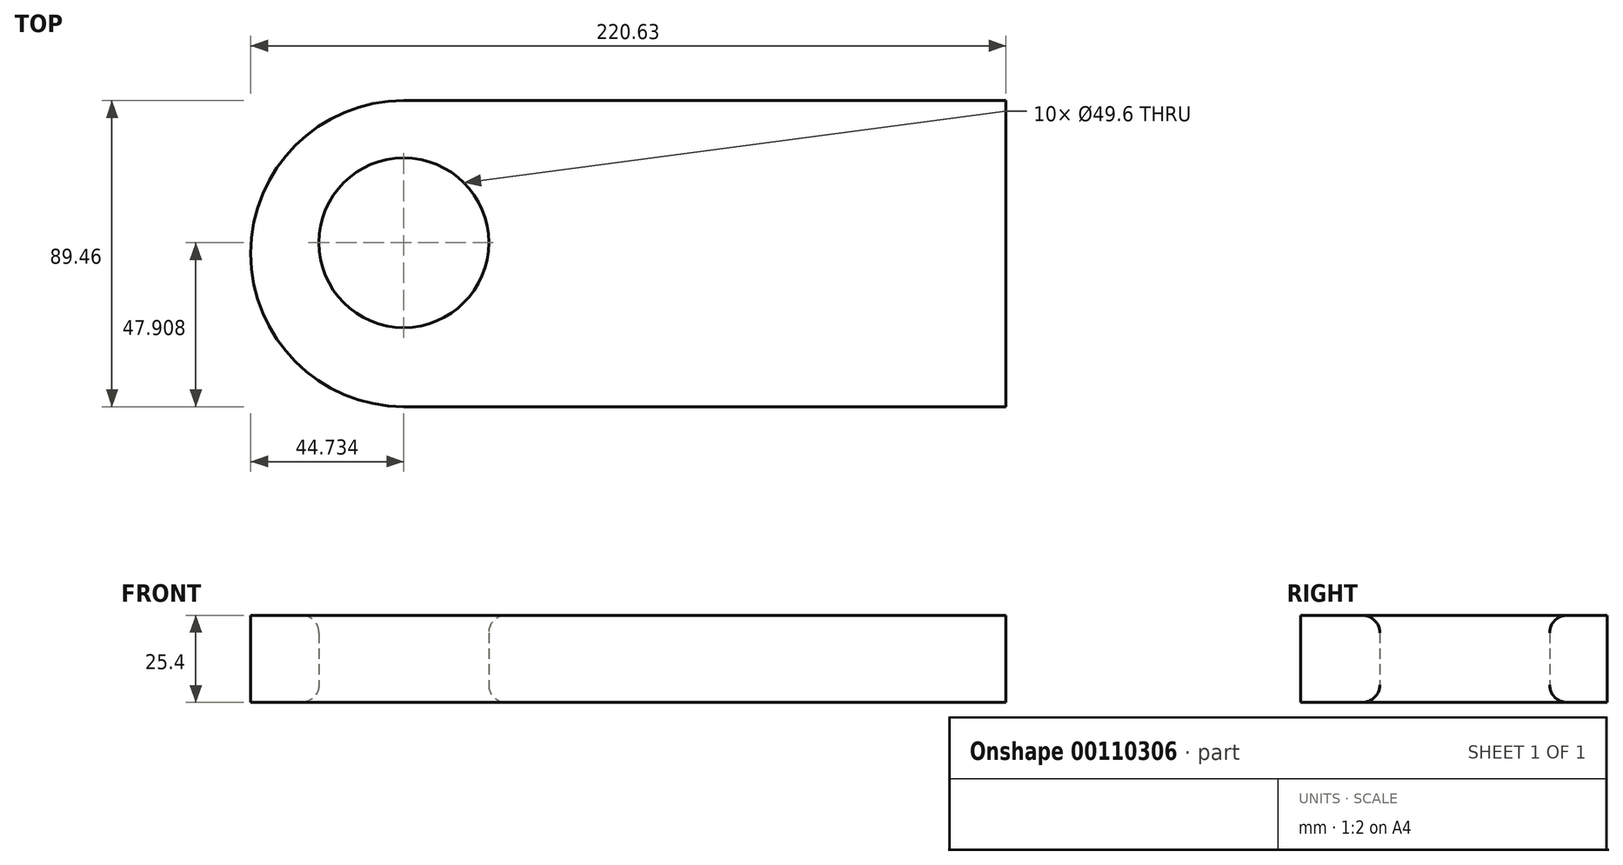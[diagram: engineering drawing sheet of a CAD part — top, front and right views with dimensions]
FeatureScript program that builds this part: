
annotation { "Feature Type Name" : "Feature", "Feature Type Description" : "" }
export const myFeature = defineFeature(function(context is Context, id is Id, definition is map)
    precondition{}
    {
        {
            var Q0;
            Q0=qCreatedBy(makeId("Top.planeOp"),FACE);
            var sketch = newSketch(context, id + "F0", { "sketchPlane" : qUnion([Q0])});
            skLineSegment(sketch, "E0.bottom", {"start": v(87.95, -44.73) * mm, "end": v(-87.95, -44.73) * mm});
            skLineSegment(sketch, "E0.top", {"start": v(87.95, 44.73) * mm, "end": v(-87.95, 44.73) * mm});
            skLineSegment(sketch, "E0.left", {"start": v(87.95, -44.73) * mm, "end": v(87.95, 44.73) * mm});
            skLineSegment(sketch, "E0.right", {"start": v(-87.95, -44.73) * mm, "end": v(-87.95, 44.73) * mm});
            skPoint(sketch, "E0.middle", {"position": v(0, 0) * mm});
            skCircle(sketch, "E1", {"center": v(-87.95, 3.18) * mm, "radius": 4.22 * mm});
            skCircle(sketch, "E2", {"center": v(-87.95, 0) * mm, "radius": 44.73 * mm});
            skCircle(sketch, "E3", {"center": v(-87.95, 3.18) * mm, "radius": 24.8 * mm});
            skSolve(sketch);
        }
        {
            var Q0;
            Q0 = qSketchRegion(id + "F0", true);
            extrude(context, id + "F1", {"entities" : qUnion([Q0]), "depth" : 25.4 * mm});
        }
        {
            var Q0;
            Q0=makeQuery(id+"F1.opExtrude","SWEPT_FACE",FACE,{"disambiguationData":[OSD([sQuery(id+"F0.wireOp",EDGE,"E3")])]});
            fillet(context, id + "F2", {"entities" : qUnion([Q0]), "radius" : 5.08 * mm, "tangentPropagation" : true, "allowEdgeOverflow" : false});
        }
    });
